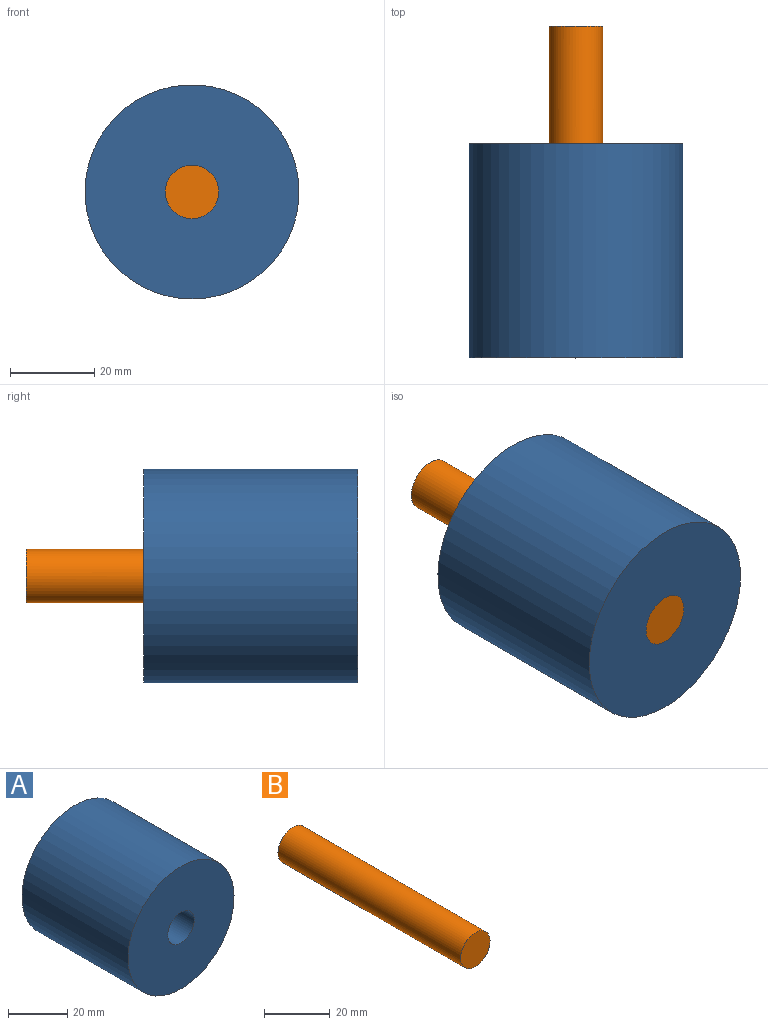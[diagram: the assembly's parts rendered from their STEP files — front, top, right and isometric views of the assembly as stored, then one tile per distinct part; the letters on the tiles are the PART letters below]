
ASSEMBLY  parts=2 mates=1
PART A: 4 faces, bbox 50.8x50.8x50.8 mm
  f0: plane 50.8x50.8mm, normal (0,-1,0), area 1900.2mm2, adj f2,f3
  f1: plane 50.8x50.8mm, normal (0,1,0), area 1900.2mm2, adj f2,f3
  f2: cylinder r=25.4mm len=50.8mm, axis (0,-1,0), area 8107.3mm2, adj f0,f1
  f3: cylinder r=6.35mm len=50.8mm, axis (0,-1,0), area 2026.8mm2, adj f0,f1
PART B: 3 faces, bbox 12.7x78.7x12.7 mm
  f0: plane 12.7x12.7mm, normal (0,1,0), area 126.7mm2, adj f1
  f1: cylinder r=6.35mm len=78.74mm, axis (0,-1,0), area 3141.6mm2, adj f0,f2
  f2: plane 12.7x12.7mm, normal (0,-1,0), area 126.7mm2, adj f1
PLACE A t=(19.67,19.18,4.96)mm
PLACE B t=(19.67,19.18,4.96)mm
MATE fastened A.f3 <-> B.f1  axis (0,-1,0) through (19.67,-16.9,4.96)mm
